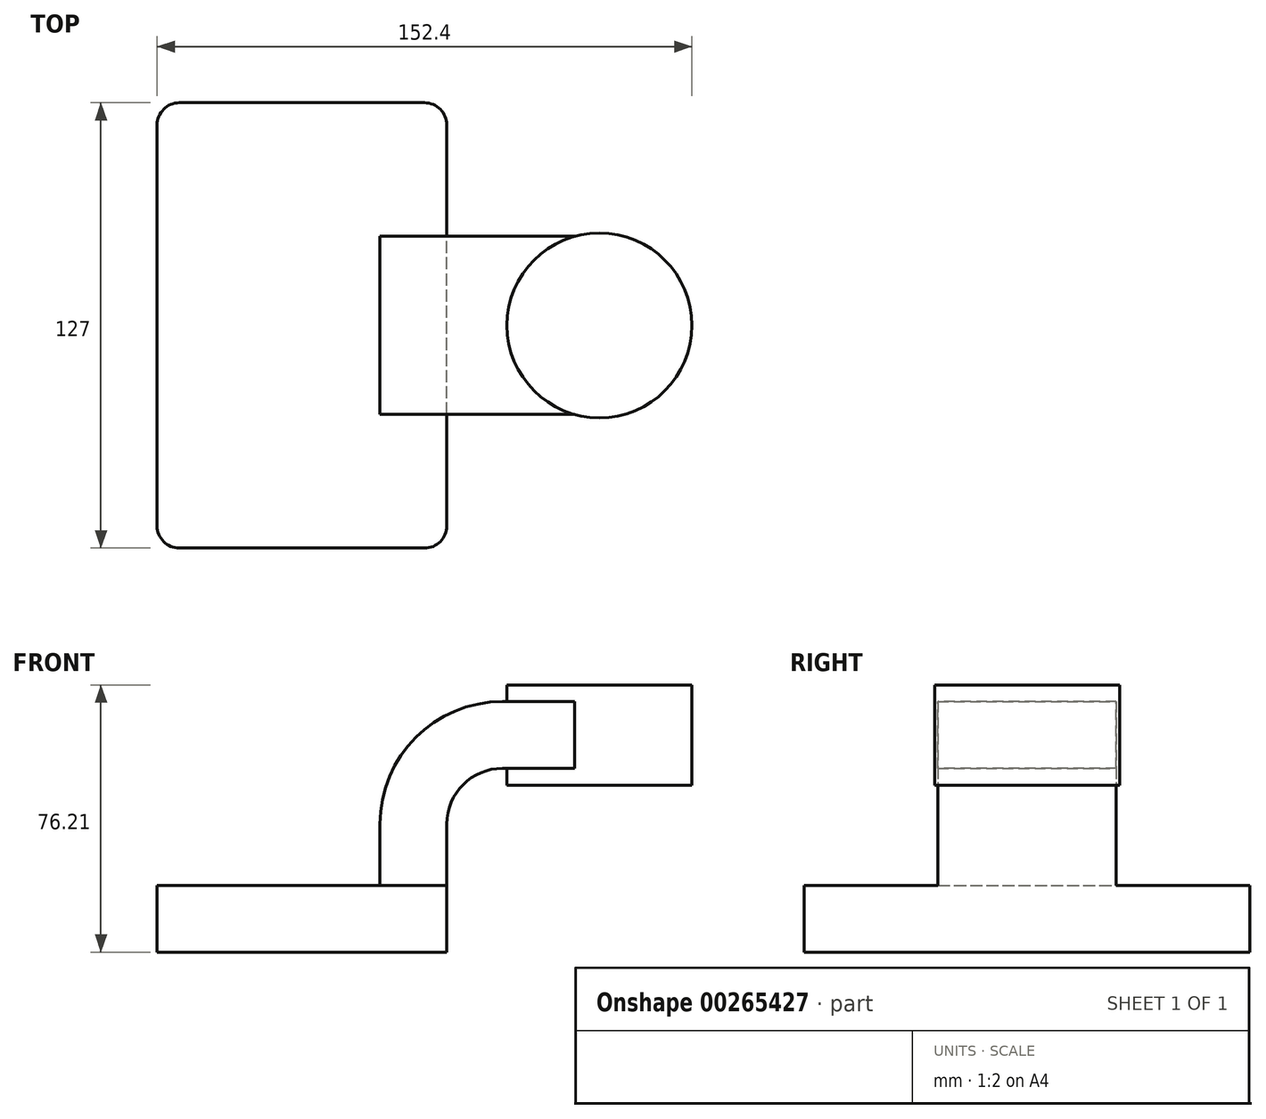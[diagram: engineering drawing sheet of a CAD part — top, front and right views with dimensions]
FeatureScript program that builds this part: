
annotation { "Feature Type Name" : "Feature", "Feature Type Description" : "" }
export const myFeature = defineFeature(function(context is Context, id is Id, definition is map)
    precondition{}
    {
        {
            var Q0;
            Q0=qCreatedBy(makeId("Front.planeOp"),FACE);
            var sketch = newSketch(context, id + "F0", { "sketchPlane" : qUnion([Q0])});
            skLineSegment(sketch, "E0.bottom", {"start": v(41.28, -9.53) * mm, "end": v(-41.27, -9.53) * mm});
            skLineSegment(sketch, "E0.top", {"start": v(41.27, 9.53) * mm, "end": v(-41.28, 9.53) * mm});
            skLineSegment(sketch, "E0.left", {"start": v(41.28, -9.52) * mm, "end": v(41.28, 9.53) * mm});
            skLineSegment(sketch, "E0.right", {"start": v(-41.28, -9.53) * mm, "end": v(-41.28, 9.53) * mm});
            skPoint(sketch, "E0.middle", {"position": v(0, 0) * mm});
            skLineSegment(sketch, "E1.bottom", {"start": v(111.12, 38.1) * mm, "end": v(60.32, 38.1) * mm});
            skLineSegment(sketch, "E1.top", {"start": v(111.12, 66.68) * mm, "end": v(60.32, 66.68) * mm});
            skLineSegment(sketch, "E1.left", {"start": v(111.12, 38.1) * mm, "end": v(111.12, 66.68) * mm});
            skLineSegment(sketch, "E1.right", {"start": v(60.32, 38.1) * mm, "end": v(60.32, 66.68) * mm});
            skPoint(sketch, "E1.middle", {"position": v(85.72, 52.39) * mm});
            skLineSegment(sketch, "E2", {"start": v(41.28, 9.53) * mm, "end": v(41.28, 27) * mm});
            skArc(sketch, "E3", {"start": v(41.27, 27) * mm, "mid": v(45.92, 38.23) * mm, "end": v(57.15, 42.88) * mm});
            skLineSegment(sketch, "E4", {"start": v(57.15, 42.88) * mm, "end": v(84.77, 42.88) * mm});
            skLineSegment(sketch, "E5.0", {"start": v(57.15, 61.93) * mm, "end": v(84.77, 61.93) * mm});
            skArc(sketch, "E5.1", {"start": v(22.23, 27) * mm, "mid": v(32.45, 51.7) * mm, "end": v(57.15, 61.93) * mm});
            skLineSegment(sketch, "E5.2", {"start": v(22.22, 9.53) * mm, "end": v(22.22, 27) * mm});
            skFitSpline(sketch, "E6", {"points": [v(-41.28, 9.53) * mm, v(57.15, 61.93) * mm], "startDerivative": vector(0, 65.98) * mm, "endDerivative": vector(152.4, 0) * mm});
            skLineSegment(sketch, "E7", {"start": v(84.77, 66.68) * mm, "end": v(84.77, 38.1) * mm});
            skSolve(sketch);
        }
        {
            var Q0;
            Q0=makeQuery(id+"F0.imprint","IMPRINT",FACE,{"disambiguationData":[TD([[makeQuery(id+"F0.imprint","IMPRINT",EDGE,{"derivedFrom":sQuery(id+"F0.wireOp",EDGE,"E0.bottom")}),-1.0]])]});
            extrude(context, id + "F1", {"entities" : qUnion([Q0]), "endBound" : BoundingType.SYMMETRIC, "depth" : 127 * mm});
        }
        {
            var Q0;
            {var subQ1=sQuery(id+"F0.wireOp",EDGE,"E2");Q0=makeQuery(id+"F0.imprint","IMPRINT",FACE,{"disambiguationData":[TD([[makeQuery(id+"F0.imprint","IMPRINT",EDGE,{"derivedFrom":subQ1}),1.0]])]});}
            var Q1;
            {var subQ0=sQuery(id+"F0.wireOp",EDGE,"E4");var subQ1=sQuery(id+"F0.wireOp",EDGE,"E1.right");var subQ2=makeQuery(id+"F0.imprint","INTERSECT",VERTEX,{"derivedFrom":[subQ1,subQ0]});Q1=makeQuery(id+"F0.imprint","IMPRINT",FACE,{"disambiguationData":[TD([[makeQuery(id+"F0.imprint","IMPRINT",EDGE,{"disambiguationData":[TD([[subQ2,-1.0]])],"derivedFrom":subQ1}),-1.0]])]});}
            extrude(context, id + "F2", {"entities" : qUnion([Q0, Q1]), "operationType" : NewBodyOperationType.ADD, "endBound" : BoundingType.SYMMETRIC, "depth" : 50.8 * mm});
        }
        {
            var Q0;
            Q0=makeQuery(id+"F0.imprint","IMPRINT",FACE,{"disambiguationData":[TD([[makeQuery(id+"F0.imprint","IMPRINT",EDGE,{"derivedFrom":sQuery(id+"F0.wireOp",EDGE,"E5.1")}),1.0]])]});
            extrude(context, id + "F3", {"entities" : qUnion([Q0]), "operationType" : NewBodyOperationType.ADD, "endBound" : BoundingType.SYMMETRIC, "depth" : 15.88 * mm});
        }
        {
            var Q0;
            {var subQ0=sQuery(id+"F0.wireOp",EDGE,"E1.left");Q0=makeQuery(id+"F0.imprint","IMPRINT",FACE,{"disambiguationData":[TD([[makeQuery(id+"F0.imprint","IMPRINT",EDGE,{"derivedFrom":subQ0}),1.0]])]});}
            var Q1;
            Q1=sQuery(id+"F0.wireOp",EDGE,"E7");
            revolve(context, id + "F4", {"operationType" : NewBodyOperationType.ADD, "entities" : qUnion([Q0]), "axis" : qUnion([Q1]), "revolveType" : RevolveType.FULL});
        }
        {
            var Q0;
            Q0=makeQuery(id+"F1.opExtrude","CAP_EDGE",EDGE,{"disambiguationData":[OSD([sQuery(id+"F0.wireOp",EDGE,"E0.left")])],"isStart":false});
            var Q1;
            Q1=makeQuery(id+"F1.opExtrude","CAP_EDGE",EDGE,{"disambiguationData":[OSD([sQuery(id+"F0.wireOp",EDGE,"E0.right")])],"isStart":false});
            var Q2;
            Q2=makeQuery(id+"F1.opExtrude","CAP_EDGE",EDGE,{"disambiguationData":[OSD([sQuery(id+"F0.wireOp",EDGE,"E0.left")])],"isStart":true});
            var Q3;
            Q3=makeQuery(id+"F1.opExtrude","CAP_EDGE",EDGE,{"disambiguationData":[OSD([sQuery(id+"F0.wireOp",EDGE,"E0.right")])],"isStart":true});
            fillet(context, id + "F5", {"entities" : qUnion([Q0, Q1, Q2, Q3]), "radius" : 6.35 * mm, "tangentPropagation" : true, "allowEdgeOverflow" : false});
        }
    });
